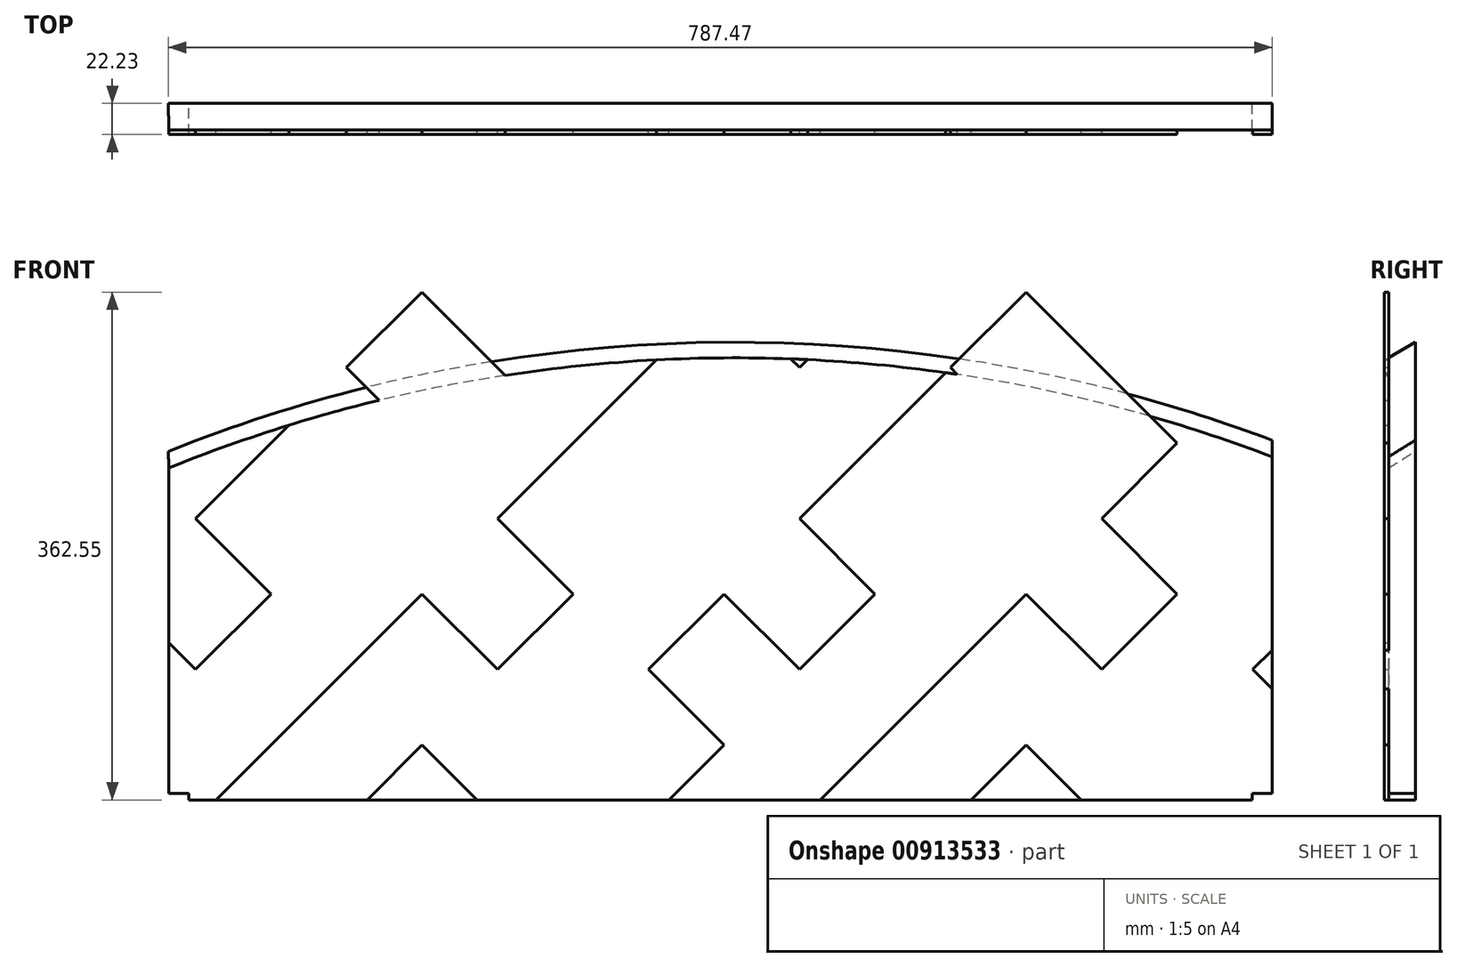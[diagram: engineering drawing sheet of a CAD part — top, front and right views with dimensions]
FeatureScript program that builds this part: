
annotation { "Feature Type Name" : "Feature", "Feature Type Description" : "" }
export const myFeature = defineFeature(function(context is Context, id is Id, definition is map)
    precondition{}
    {
        {
            var Q0;
            Q0=qCreatedBy(makeId("Front.planeOp"),FACE);
            var sketch = newSketch(context, id + "F0", { "sketchPlane" : qUnion([Q0])});
            skLineSegment(sketch, "E0.bottom", {"start": v(393.7, 124.62) * mm, "end": v(-393.67, 118.27) * mm, "construction": true});
            skLineSegment(sketch, "E0.top", {"start": v(379.41, -118.27) * mm, "end": v(-379.39, -118.27) * mm});
            skLineSegment(sketch, "E0.left", {"start": v(393.7, 124.62) * mm, "end": v(393.7, -113.5) * mm});
            skLineSegment(sketch, "E0.right", {"start": v(-393.67, 118.27) * mm, "end": v(-393.67, -113.5) * mm});
            skPoint(sketch, "E0.middle", {"position": v(0, 0) * mm});
            skLineSegment(sketch, "E1", {"start": v(379.41, -118.27) * mm, "end": v(379.41, -113.5) * mm});
            skLineSegment(sketch, "E2", {"start": v(379.41, -113.5) * mm, "end": v(393.7, -113.5) * mm});
            skPoint(sketch, "E3.orphan", {"position": v(393.67, -118.27) * mm});
            skLineSegment(sketch, "E4", {"start": v(-393.67, -113.5) * mm, "end": v(-379.39, -113.5) * mm});
            skLineSegment(sketch, "E5", {"start": v(-379.39, -113.5) * mm, "end": v(-379.39, -118.27) * mm});
            skLineSegment(sketch, "E6", {"start": v(0, 121.44) * mm, "end": v(-0.6, 196.06) * mm, "construction": true});
            skArc(sketch, "E7", {"start": v(393.7, 124.62) * mm, "mid": v(-0.59, 196.06) * mm, "end": v(-393.67, 118.27) * mm});
            skPoint(sketch, "E7.third.point", {"position": v(1080.75, -964.13) * mm});
            skLineSegment(sketch, "E8", {"start": v(-0.6, 196.06) * mm, "end": v(-0.6, 208.76) * mm, "construction": true});
            skLineSegment(sketch, "E9", {"start": v(-393.67, 118.27) * mm, "end": v(-393.78, 130.97) * mm});
            skLineSegment(sketch, "E10", {"start": v(393.7, 124.62) * mm, "end": v(393.7, 138.9) * mm});
            skArc(sketch, "E11", {"start": v(393.7, 138.9) * mm, "mid": v(-0.78, 208.75) * mm, "end": v(-393.78, 130.97) * mm});
            skSolve(sketch);
        }
        {
            var Q0;
            Q0=makeQuery(id+"F0.imprint","IMPRINT",FACE,{"disambiguationData":[TD([[makeQuery(id+"F0.imprint","IMPRINT",EDGE,{"derivedFrom":sQuery(id+"F0.wireOp",EDGE,"E0.top")}),-1.0]])]});
            var Q1;
            Q1=makeQuery(id+"F0.imprint","IMPRINT",FACE,{"disambiguationData":[TD([[makeQuery(id+"F0.imprint","IMPRINT",EDGE,{"derivedFrom":sQuery(id+"F0.wireOp",EDGE,"E7")}),-1.0]])]});
            extrude(context, id + "F1", {"entities" : qUnion([Q0, Q1]), "depth" : 19.05 * mm, "offsetDistance" : 25.4 * mm});
        }
        {
            var Q0;
            Q0=makeQuery(id+"F1.opExtrude","CAP_EDGE",EDGE,{"disambiguationData":[OSD([sQuery(id+"F0.wireOp",EDGE,"E11")])],"isStart":false});
            chamfer(context, id + "F2", {"entities" : qUnion([Q0]), "chamferType" : ChamferType.TWO_OFFSETS, "width1" : 19.56 * mm, "oppositeDirection" : true, "width2" : 11.43 * mm, "tangentPropagation" : true});
        }
        {
            var Q0;
            Q0=makeQuery(id+"F1.opExtrude","CAP_FACE",FACE,{"disambiguationData":[OSD([sQuery(id+"F0.wireOp",EDGE,"E0.top"),sQuery(id+"F0.wireOp",EDGE,"E0.left"),sQuery(id+"F0.wireOp",EDGE,"E0.right"),sQuery(id+"F0.wireOp",EDGE,"E1"),sQuery(id+"F0.wireOp",EDGE,"E2"),sQuery(id+"F0.wireOp",EDGE,"E4"),sQuery(id+"F0.wireOp",EDGE,"E5"),sQuery(id+"F0.wireOp",EDGE,"E9"),sQuery(id+"F0.wireOp",EDGE,"E10"),sQuery(id+"F0.wireOp",EDGE,"E11")])],"isStart":false});
            var sketch = newSketch(context, id + "F3", { "sketchPlane" : qUnion([Q0])});
            skLineSegment(sketch, "E12.bottom", {"start": v(272.06, -779.44) * mm, "end": v(325.94, -725.56) * mm});
            skLineSegment(sketch, "E12.top", {"start": v(164.3, -671.68) * mm, "end": v(218.17, -617.8) * mm});
            skLineSegment(sketch, "E12.left", {"start": v(272.06, -779.44) * mm, "end": v(164.3, -671.68) * mm});
            skLineSegment(sketch, "E12.right", {"start": v(325.94, -725.56) * mm, "end": v(218.17, -617.8) * mm});
            skLineSegment(sketch, "E13.bottom", {"start": v(433.7, -617.8) * mm, "end": v(379.82, -563.91) * mm});
            skLineSegment(sketch, "E13.top", {"start": v(325.94, -725.56) * mm, "end": v(272.06, -671.68) * mm});
            skLineSegment(sketch, "E13.left", {"start": v(433.7, -617.8) * mm, "end": v(325.94, -725.56) * mm});
            skLineSegment(sketch, "E13.right", {"start": v(379.82, -563.91) * mm, "end": v(272.06, -671.68) * mm});
            skLineSegment(sketch, "E14.bottom", {"start": v(272.06, -671.68) * mm, "end": v(325.94, -617.8) * mm});
            skLineSegment(sketch, "E14.top", {"start": v(164.3, -563.91) * mm, "end": v(218.17, -510.03) * mm});
            skLineSegment(sketch, "E14.left", {"start": v(272.06, -671.68) * mm, "end": v(164.3, -563.91) * mm});
            skLineSegment(sketch, "E14.right", {"start": v(325.94, -617.8) * mm, "end": v(218.17, -510.03) * mm});
            skPoint(sketch, "E15", {"position": v(325.94, -617.8) * mm});
            skLineSegment(sketch, "E16.bottom", {"start": v(272.06, -563.91) * mm, "end": v(325.94, -510.03) * mm});
            skLineSegment(sketch, "E16.top", {"start": v(164.3, -456.15) * mm, "end": v(218.17, -402.27) * mm});
            skLineSegment(sketch, "E16.left", {"start": v(272.06, -563.91) * mm, "end": v(164.3, -456.15) * mm});
            skLineSegment(sketch, "E16.right", {"start": v(325.94, -510.03) * mm, "end": v(218.17, -402.27) * mm});
            skLineSegment(sketch, "E17.bottom", {"start": v(433.7, -510.03) * mm, "end": v(379.82, -456.15) * mm});
            skLineSegment(sketch, "E17.top", {"start": v(325.94, -617.8) * mm, "end": v(272.06, -563.91) * mm});
            skLineSegment(sketch, "E17.left", {"start": v(433.7, -510.03) * mm, "end": v(325.94, -617.8) * mm});
            skLineSegment(sketch, "E17.right", {"start": v(379.82, -456.15) * mm, "end": v(272.06, -563.91) * mm});
            skLineSegment(sketch, "E18.bottom", {"start": v(272.06, -456.15) * mm, "end": v(325.94, -402.27) * mm});
            skLineSegment(sketch, "E18.top", {"start": v(164.3, -348.39) * mm, "end": v(218.17, -294.5) * mm});
            skLineSegment(sketch, "E18.left", {"start": v(272.06, -456.15) * mm, "end": v(164.3, -348.39) * mm});
            skLineSegment(sketch, "E18.right", {"start": v(325.94, -402.27) * mm, "end": v(218.17, -294.5) * mm});
            skLineSegment(sketch, "E19.bottom", {"start": v(433.7, -402.27) * mm, "end": v(379.82, -348.39) * mm});
            skLineSegment(sketch, "E19.top", {"start": v(325.94, -510.03) * mm, "end": v(272.06, -456.15) * mm});
            skLineSegment(sketch, "E19.left", {"start": v(433.7, -402.27) * mm, "end": v(325.94, -510.03) * mm});
            skLineSegment(sketch, "E19.right", {"start": v(379.82, -348.39) * mm, "end": v(272.06, -456.15) * mm});
            skLineSegment(sketch, "E20.bottom", {"start": v(487.58, -563.91) * mm, "end": v(541.46, -510.03) * mm});
            skLineSegment(sketch, "E20.top", {"start": v(379.82, -456.15) * mm, "end": v(433.7, -402.27) * mm});
            skLineSegment(sketch, "E20.left", {"start": v(487.58, -563.91) * mm, "end": v(379.82, -456.15) * mm});
            skLineSegment(sketch, "E20.right", {"start": v(541.46, -510.03) * mm, "end": v(433.7, -402.27) * mm});
            skLineSegment(sketch, "E21.bottom", {"start": v(487.58, -779.44) * mm, "end": v(541.46, -725.56) * mm});
            skLineSegment(sketch, "E21.top", {"start": v(379.82, -671.68) * mm, "end": v(433.7, -617.8) * mm});
            skLineSegment(sketch, "E21.left", {"start": v(487.58, -779.44) * mm, "end": v(379.82, -671.68) * mm});
            skLineSegment(sketch, "E21.right", {"start": v(541.46, -725.56) * mm, "end": v(433.7, -617.8) * mm});
            skLineSegment(sketch, "E22.bottom", {"start": v(487.58, -671.68) * mm, "end": v(541.46, -617.8) * mm});
            skLineSegment(sketch, "E22.top", {"start": v(379.82, -563.91) * mm, "end": v(433.7, -510.03) * mm});
            skLineSegment(sketch, "E22.left", {"start": v(487.58, -671.68) * mm, "end": v(379.82, -563.91) * mm});
            skLineSegment(sketch, "E22.right", {"start": v(541.46, -617.8) * mm, "end": v(433.7, -510.03) * mm});
            skLineSegment(sketch, "E23.bottom", {"start": v(272.06, -348.39) * mm, "end": v(325.94, -294.5) * mm});
            skLineSegment(sketch, "E23.top", {"start": v(164.3, -240.63) * mm, "end": v(218.17, -186.74) * mm});
            skLineSegment(sketch, "E23.left", {"start": v(272.06, -348.39) * mm, "end": v(164.3, -240.63) * mm});
            skLineSegment(sketch, "E23.right", {"start": v(325.94, -294.5) * mm, "end": v(218.17, -186.74) * mm});
            skLineSegment(sketch, "E24.bottom", {"start": v(433.7, -294.5) * mm, "end": v(379.82, -240.63) * mm});
            skLineSegment(sketch, "E24.top", {"start": v(325.94, -402.27) * mm, "end": v(272.06, -348.39) * mm});
            skLineSegment(sketch, "E24.left", {"start": v(433.7, -294.5) * mm, "end": v(325.94, -402.27) * mm});
            skLineSegment(sketch, "E24.right", {"start": v(379.82, -240.63) * mm, "end": v(272.06, -348.39) * mm});
            skLineSegment(sketch, "E25.bottom", {"start": v(218.17, -402.27) * mm, "end": v(164.3, -348.39) * mm});
            skLineSegment(sketch, "E25.top", {"start": v(110.41, -510.03) * mm, "end": v(56.53, -456.15) * mm});
            skLineSegment(sketch, "E25.left", {"start": v(218.17, -402.27) * mm, "end": v(110.41, -510.03) * mm});
            skLineSegment(sketch, "E25.right", {"start": v(164.3, -348.39) * mm, "end": v(56.53, -456.15) * mm});
            skLineSegment(sketch, "E26.bottom", {"start": v(218.17, -294.5) * mm, "end": v(164.3, -240.63) * mm});
            skLineSegment(sketch, "E26.top", {"start": v(110.41, -402.27) * mm, "end": v(56.53, -348.39) * mm});
            skLineSegment(sketch, "E26.left", {"start": v(218.17, -294.5) * mm, "end": v(110.41, -402.27) * mm});
            skLineSegment(sketch, "E26.right", {"start": v(164.3, -240.63) * mm, "end": v(56.53, -348.39) * mm});
            skLineSegment(sketch, "E27.bottom", {"start": v(218.17, -617.8) * mm, "end": v(164.3, -563.91) * mm});
            skLineSegment(sketch, "E27.top", {"start": v(110.41, -725.56) * mm, "end": v(56.53, -671.68) * mm});
            skLineSegment(sketch, "E27.left", {"start": v(218.17, -617.8) * mm, "end": v(110.41, -725.56) * mm});
            skLineSegment(sketch, "E27.right", {"start": v(164.3, -563.91) * mm, "end": v(56.53, -671.68) * mm});
            skLineSegment(sketch, "E28.bottom", {"start": v(218.17, -510.03) * mm, "end": v(164.3, -456.15) * mm});
            skLineSegment(sketch, "E28.top", {"start": v(110.41, -617.8) * mm, "end": v(56.53, -563.91) * mm});
            skLineSegment(sketch, "E28.left", {"start": v(218.17, -510.03) * mm, "end": v(110.41, -617.8) * mm});
            skLineSegment(sketch, "E28.right", {"start": v(164.3, -456.15) * mm, "end": v(56.53, -563.91) * mm});
            skLineSegment(sketch, "E29.bottom", {"start": v(272.09, -240.66) * mm, "end": v(325.97, -186.77) * mm});
            skLineSegment(sketch, "E29.top", {"start": v(164.32, -132.9) * mm, "end": v(218.2, -79.01) * mm});
            skLineSegment(sketch, "E29.left", {"start": v(272.09, -240.66) * mm, "end": v(164.32, -132.9) * mm});
            skLineSegment(sketch, "E29.right", {"start": v(325.97, -186.77) * mm, "end": v(218.2, -79.01) * mm});
            skLineSegment(sketch, "E30.bottom", {"start": v(433.73, -79.01) * mm, "end": v(379.85, -25.13) * mm});
            skLineSegment(sketch, "E30.top", {"start": v(325.97, -186.77) * mm, "end": v(272.09, -132.9) * mm});
            skLineSegment(sketch, "E30.left", {"start": v(433.73, -79.01) * mm, "end": v(325.97, -186.77) * mm});
            skLineSegment(sketch, "E30.right", {"start": v(379.85, -25.13) * mm, "end": v(272.09, -132.9) * mm});
            skLineSegment(sketch, "E31.bottom", {"start": v(272.09, -132.9) * mm, "end": v(325.97, -79.01) * mm});
            skLineSegment(sketch, "E31.top", {"start": v(164.32, -25.13) * mm, "end": v(218.2, 28.75) * mm});
            skLineSegment(sketch, "E31.left", {"start": v(272.09, -132.9) * mm, "end": v(164.32, -25.13) * mm});
            skLineSegment(sketch, "E31.right", {"start": v(325.97, -79.01) * mm, "end": v(218.2, 28.75) * mm});
            skPoint(sketch, "E32", {"position": v(325.97, -79.01) * mm});
            skLineSegment(sketch, "E33.bottom", {"start": v(272.09, -25.13) * mm, "end": v(325.97, 28.75) * mm});
            skLineSegment(sketch, "E33.top", {"start": v(164.32, 82.63) * mm, "end": v(218.2, 136.52) * mm});
            skLineSegment(sketch, "E33.left", {"start": v(272.09, -25.13) * mm, "end": v(164.32, 82.63) * mm});
            skLineSegment(sketch, "E33.right", {"start": v(325.97, 28.75) * mm, "end": v(218.2, 136.52) * mm});
            skLineSegment(sketch, "E34.bottom", {"start": v(433.73, 28.75) * mm, "end": v(379.85, 82.63) * mm});
            skLineSegment(sketch, "E34.top", {"start": v(325.97, -79.01) * mm, "end": v(272.09, -25.13) * mm});
            skLineSegment(sketch, "E34.left", {"start": v(433.73, 28.75) * mm, "end": v(325.97, -79.01) * mm});
            skLineSegment(sketch, "E34.right", {"start": v(379.85, 82.63) * mm, "end": v(272.09, -25.13) * mm});
            skLineSegment(sketch, "E35.bottom", {"start": v(272.09, 82.63) * mm, "end": v(325.97, 136.52) * mm});
            skLineSegment(sketch, "E35.top", {"start": v(164.32, 190.4) * mm, "end": v(218.2, 244.28) * mm});
            skLineSegment(sketch, "E35.left", {"start": v(272.09, 82.63) * mm, "end": v(164.32, 190.4) * mm});
            skLineSegment(sketch, "E35.right", {"start": v(325.97, 136.52) * mm, "end": v(218.2, 244.28) * mm});
            skLineSegment(sketch, "E36.bottom", {"start": v(433.73, 136.52) * mm, "end": v(379.85, 190.4) * mm});
            skLineSegment(sketch, "E36.top", {"start": v(325.97, 28.75) * mm, "end": v(272.09, 82.63) * mm});
            skLineSegment(sketch, "E36.left", {"start": v(433.73, 136.52) * mm, "end": v(325.97, 28.75) * mm});
            skLineSegment(sketch, "E36.right", {"start": v(379.85, 190.4) * mm, "end": v(272.09, 82.63) * mm});
            skLineSegment(sketch, "E37.bottom", {"start": v(487.61, -25.13) * mm, "end": v(541.5, 28.75) * mm});
            skLineSegment(sketch, "E37.top", {"start": v(379.85, 82.63) * mm, "end": v(433.73, 136.52) * mm});
            skLineSegment(sketch, "E37.left", {"start": v(487.61, -25.13) * mm, "end": v(379.85, 82.63) * mm});
            skLineSegment(sketch, "E37.right", {"start": v(541.5, 28.75) * mm, "end": v(433.73, 136.52) * mm});
            skLineSegment(sketch, "E38.bottom", {"start": v(487.61, -240.66) * mm, "end": v(541.5, -186.77) * mm});
            skLineSegment(sketch, "E38.top", {"start": v(379.85, -132.9) * mm, "end": v(433.73, -79.01) * mm});
            skLineSegment(sketch, "E38.left", {"start": v(487.61, -240.66) * mm, "end": v(379.85, -132.9) * mm});
            skLineSegment(sketch, "E38.right", {"start": v(541.5, -186.77) * mm, "end": v(433.73, -79.01) * mm});
            skLineSegment(sketch, "E39.bottom", {"start": v(487.61, -132.9) * mm, "end": v(541.5, -79.01) * mm});
            skLineSegment(sketch, "E39.top", {"start": v(379.85, -25.13) * mm, "end": v(433.73, 28.75) * mm});
            skLineSegment(sketch, "E39.left", {"start": v(487.61, -132.9) * mm, "end": v(379.85, -25.13) * mm});
            skLineSegment(sketch, "E39.right", {"start": v(541.5, -79.01) * mm, "end": v(433.73, 28.75) * mm});
            skLineSegment(sketch, "E40.bottom", {"start": v(272.09, 190.4) * mm, "end": v(325.97, 244.28) * mm});
            skLineSegment(sketch, "E40.top", {"start": v(164.32, 298.16) * mm, "end": v(218.2, 352.04) * mm});
            skLineSegment(sketch, "E40.left", {"start": v(272.09, 190.4) * mm, "end": v(164.32, 298.16) * mm});
            skLineSegment(sketch, "E40.right", {"start": v(325.97, 244.28) * mm, "end": v(218.2, 352.04) * mm});
            skLineSegment(sketch, "E41.bottom", {"start": v(433.73, 244.28) * mm, "end": v(379.85, 298.16) * mm});
            skLineSegment(sketch, "E41.top", {"start": v(325.97, 136.52) * mm, "end": v(272.09, 190.4) * mm});
            skLineSegment(sketch, "E41.left", {"start": v(433.73, 244.28) * mm, "end": v(325.97, 136.52) * mm});
            skLineSegment(sketch, "E41.right", {"start": v(379.85, 298.16) * mm, "end": v(272.09, 190.4) * mm});
            skLineSegment(sketch, "E42.bottom", {"start": v(218.2, 136.52) * mm, "end": v(164.32, 190.4) * mm});
            skLineSegment(sketch, "E42.top", {"start": v(110.44, 28.75) * mm, "end": v(56.56, 82.63) * mm});
            skLineSegment(sketch, "E42.left", {"start": v(218.2, 136.52) * mm, "end": v(110.44, 28.75) * mm});
            skLineSegment(sketch, "E42.right", {"start": v(164.32, 190.4) * mm, "end": v(56.56, 82.63) * mm});
            skLineSegment(sketch, "E43.bottom", {"start": v(218.2, 244.28) * mm, "end": v(164.32, 298.16) * mm});
            skLineSegment(sketch, "E43.top", {"start": v(110.44, 136.52) * mm, "end": v(56.56, 190.4) * mm});
            skLineSegment(sketch, "E43.left", {"start": v(218.2, 244.28) * mm, "end": v(110.44, 136.52) * mm});
            skLineSegment(sketch, "E43.right", {"start": v(164.32, 298.16) * mm, "end": v(56.56, 190.4) * mm});
            skLineSegment(sketch, "E44.bottom", {"start": v(218.2, -79.01) * mm, "end": v(164.32, -25.13) * mm});
            skLineSegment(sketch, "E44.top", {"start": v(110.44, -186.77) * mm, "end": v(56.56, -132.9) * mm});
            skLineSegment(sketch, "E44.left", {"start": v(218.2, -79.01) * mm, "end": v(110.44, -186.77) * mm});
            skLineSegment(sketch, "E44.right", {"start": v(164.32, -25.13) * mm, "end": v(56.56, -132.9) * mm});
            skLineSegment(sketch, "E45.bottom", {"start": v(218.2, 28.75) * mm, "end": v(164.32, 82.63) * mm});
            skLineSegment(sketch, "E45.top", {"start": v(110.44, -79.01) * mm, "end": v(56.56, -25.13) * mm});
            skLineSegment(sketch, "E45.left", {"start": v(218.2, 28.75) * mm, "end": v(110.44, -79.01) * mm});
            skLineSegment(sketch, "E45.right", {"start": v(164.32, 82.63) * mm, "end": v(56.56, -25.13) * mm});
            skLineSegment(sketch, "E46.bottom", {"start": v(433.7, -186.74) * mm, "end": v(379.82, -132.86) * mm});
            skLineSegment(sketch, "E46.top", {"start": v(325.94, -294.5) * mm, "end": v(272.06, -240.63) * mm});
            skLineSegment(sketch, "E46.left", {"start": v(433.7, -186.74) * mm, "end": v(325.94, -294.5) * mm});
            skLineSegment(sketch, "E46.right", {"start": v(379.82, -132.86) * mm, "end": v(272.06, -240.63) * mm});
            skLineSegment(sketch, "E47.bottom", {"start": v(-159, -779.44) * mm, "end": v(-105.11, -725.56) * mm});
            skLineSegment(sketch, "E47.top", {"start": v(-266.76, -671.68) * mm, "end": v(-212.88, -617.8) * mm});
            skLineSegment(sketch, "E47.left", {"start": v(-159, -779.44) * mm, "end": v(-266.76, -671.68) * mm});
            skLineSegment(sketch, "E47.right", {"start": v(-105.11, -725.56) * mm, "end": v(-212.88, -617.8) * mm});
            skLineSegment(sketch, "E48.bottom", {"start": v(2.65, -617.8) * mm, "end": v(-51.23, -563.91) * mm});
            skLineSegment(sketch, "E48.top", {"start": v(-105.11, -725.56) * mm, "end": v(-159, -671.68) * mm});
            skLineSegment(sketch, "E48.left", {"start": v(2.65, -617.8) * mm, "end": v(-105.11, -725.56) * mm});
            skLineSegment(sketch, "E48.right", {"start": v(-51.23, -563.91) * mm, "end": v(-159, -671.68) * mm});
            skLineSegment(sketch, "E49.bottom", {"start": v(-159, -671.68) * mm, "end": v(-105.11, -617.8) * mm});
            skLineSegment(sketch, "E49.top", {"start": v(-266.76, -563.91) * mm, "end": v(-212.88, -510.03) * mm});
            skLineSegment(sketch, "E49.left", {"start": v(-159, -671.68) * mm, "end": v(-266.76, -563.91) * mm});
            skLineSegment(sketch, "E49.right", {"start": v(-105.11, -617.8) * mm, "end": v(-212.88, -510.03) * mm});
            skPoint(sketch, "E50", {"position": v(-105.11, -617.8) * mm});
            skLineSegment(sketch, "E51.bottom", {"start": v(-159, -563.91) * mm, "end": v(-105.11, -510.03) * mm});
            skLineSegment(sketch, "E51.top", {"start": v(-266.76, -456.15) * mm, "end": v(-212.88, -402.27) * mm});
            skLineSegment(sketch, "E51.left", {"start": v(-159, -563.91) * mm, "end": v(-266.76, -456.15) * mm});
            skLineSegment(sketch, "E51.right", {"start": v(-105.11, -510.03) * mm, "end": v(-212.88, -402.27) * mm});
            skLineSegment(sketch, "E52.bottom", {"start": v(2.65, -510.03) * mm, "end": v(-51.23, -456.15) * mm});
            skLineSegment(sketch, "E52.top", {"start": v(-105.11, -617.8) * mm, "end": v(-159, -563.91) * mm});
            skLineSegment(sketch, "E52.left", {"start": v(2.65, -510.03) * mm, "end": v(-105.11, -617.8) * mm});
            skLineSegment(sketch, "E52.right", {"start": v(-51.23, -456.15) * mm, "end": v(-159, -563.91) * mm});
            skLineSegment(sketch, "E53.bottom", {"start": v(-159, -456.15) * mm, "end": v(-105.11, -402.27) * mm});
            skLineSegment(sketch, "E53.top", {"start": v(-266.76, -348.39) * mm, "end": v(-212.88, -294.5) * mm});
            skLineSegment(sketch, "E53.left", {"start": v(-159, -456.15) * mm, "end": v(-266.76, -348.39) * mm});
            skLineSegment(sketch, "E53.right", {"start": v(-105.11, -402.27) * mm, "end": v(-212.88, -294.5) * mm});
            skLineSegment(sketch, "E54.bottom", {"start": v(2.65, -402.27) * mm, "end": v(-51.23, -348.39) * mm});
            skLineSegment(sketch, "E54.top", {"start": v(-105.11, -510.03) * mm, "end": v(-159, -456.15) * mm});
            skLineSegment(sketch, "E54.left", {"start": v(2.65, -402.27) * mm, "end": v(-105.11, -510.03) * mm});
            skLineSegment(sketch, "E54.right", {"start": v(-51.23, -348.39) * mm, "end": v(-159, -456.15) * mm});
            skLineSegment(sketch, "E55.bottom", {"start": v(56.53, -563.91) * mm, "end": v(110.41, -510.03) * mm});
            skLineSegment(sketch, "E55.top", {"start": v(-51.23, -456.15) * mm, "end": v(2.65, -402.27) * mm});
            skLineSegment(sketch, "E55.left", {"start": v(56.53, -563.91) * mm, "end": v(-51.23, -456.15) * mm});
            skLineSegment(sketch, "E55.right", {"start": v(110.41, -510.03) * mm, "end": v(2.65, -402.27) * mm});
            skLineSegment(sketch, "E56.bottom", {"start": v(56.53, -779.44) * mm, "end": v(110.41, -725.56) * mm});
            skLineSegment(sketch, "E56.top", {"start": v(-51.23, -671.68) * mm, "end": v(2.65, -617.8) * mm});
            skLineSegment(sketch, "E56.left", {"start": v(56.53, -779.44) * mm, "end": v(-51.23, -671.68) * mm});
            skLineSegment(sketch, "E56.right", {"start": v(110.41, -725.56) * mm, "end": v(2.65, -617.8) * mm});
            skLineSegment(sketch, "E57.bottom", {"start": v(56.53, -671.68) * mm, "end": v(110.41, -617.8) * mm});
            skLineSegment(sketch, "E57.top", {"start": v(-51.23, -563.91) * mm, "end": v(2.65, -510.03) * mm});
            skLineSegment(sketch, "E57.left", {"start": v(56.53, -671.68) * mm, "end": v(-51.23, -563.91) * mm});
            skLineSegment(sketch, "E57.right", {"start": v(110.41, -617.8) * mm, "end": v(2.65, -510.03) * mm});
            skLineSegment(sketch, "E58.bottom", {"start": v(-159, -348.39) * mm, "end": v(-105.11, -294.5) * mm});
            skLineSegment(sketch, "E58.top", {"start": v(-266.76, -240.63) * mm, "end": v(-212.88, -186.74) * mm});
            skLineSegment(sketch, "E58.left", {"start": v(-159, -348.39) * mm, "end": v(-266.76, -240.63) * mm});
            skLineSegment(sketch, "E58.right", {"start": v(-105.11, -294.5) * mm, "end": v(-212.88, -186.74) * mm});
            skLineSegment(sketch, "E59.bottom", {"start": v(2.65, -294.5) * mm, "end": v(-51.23, -240.63) * mm});
            skLineSegment(sketch, "E59.top", {"start": v(-105.11, -402.27) * mm, "end": v(-159, -348.39) * mm});
            skLineSegment(sketch, "E59.left", {"start": v(2.65, -294.5) * mm, "end": v(-105.11, -402.27) * mm});
            skLineSegment(sketch, "E59.right", {"start": v(-51.23, -240.63) * mm, "end": v(-159, -348.39) * mm});
            skLineSegment(sketch, "E60.bottom", {"start": v(-212.88, -402.27) * mm, "end": v(-266.76, -348.39) * mm});
            skLineSegment(sketch, "E60.top", {"start": v(-320.64, -510.03) * mm, "end": v(-374.52, -456.15) * mm});
            skLineSegment(sketch, "E60.left", {"start": v(-212.88, -402.27) * mm, "end": v(-320.64, -510.03) * mm});
            skLineSegment(sketch, "E60.right", {"start": v(-266.76, -348.39) * mm, "end": v(-374.52, -456.15) * mm});
            skLineSegment(sketch, "E61.bottom", {"start": v(-212.88, -294.5) * mm, "end": v(-266.76, -240.63) * mm});
            skLineSegment(sketch, "E61.top", {"start": v(-320.64, -402.27) * mm, "end": v(-374.52, -348.39) * mm});
            skLineSegment(sketch, "E61.left", {"start": v(-212.88, -294.5) * mm, "end": v(-320.64, -402.27) * mm});
            skLineSegment(sketch, "E61.right", {"start": v(-266.76, -240.63) * mm, "end": v(-374.52, -348.39) * mm});
            skLineSegment(sketch, "E62.bottom", {"start": v(-212.88, -617.8) * mm, "end": v(-266.76, -563.91) * mm});
            skLineSegment(sketch, "E62.top", {"start": v(-320.64, -725.56) * mm, "end": v(-374.52, -671.68) * mm});
            skLineSegment(sketch, "E62.left", {"start": v(-212.88, -617.8) * mm, "end": v(-320.64, -725.56) * mm});
            skLineSegment(sketch, "E62.right", {"start": v(-266.76, -563.91) * mm, "end": v(-374.52, -671.68) * mm});
            skLineSegment(sketch, "E63.bottom", {"start": v(-212.88, -510.03) * mm, "end": v(-266.76, -456.15) * mm});
            skLineSegment(sketch, "E63.top", {"start": v(-320.64, -617.8) * mm, "end": v(-374.52, -563.91) * mm});
            skLineSegment(sketch, "E63.left", {"start": v(-212.88, -510.03) * mm, "end": v(-320.64, -617.8) * mm});
            skLineSegment(sketch, "E63.right", {"start": v(-266.76, -456.15) * mm, "end": v(-374.52, -563.91) * mm});
            skLineSegment(sketch, "E64.bottom", {"start": v(-158.97, -240.66) * mm, "end": v(-105.08, -186.77) * mm});
            skLineSegment(sketch, "E64.top", {"start": v(-266.73, -132.9) * mm, "end": v(-212.85, -79.01) * mm});
            skLineSegment(sketch, "E64.left", {"start": v(-158.97, -240.66) * mm, "end": v(-266.73, -132.9) * mm});
            skLineSegment(sketch, "E64.right", {"start": v(-105.08, -186.77) * mm, "end": v(-212.85, -79.01) * mm});
            skLineSegment(sketch, "E65.bottom", {"start": v(2.68, -79.01) * mm, "end": v(-51.2, -25.13) * mm});
            skLineSegment(sketch, "E65.top", {"start": v(-105.08, -186.77) * mm, "end": v(-158.97, -132.9) * mm});
            skLineSegment(sketch, "E65.left", {"start": v(2.68, -79.01) * mm, "end": v(-105.08, -186.77) * mm});
            skLineSegment(sketch, "E65.right", {"start": v(-51.2, -25.13) * mm, "end": v(-158.97, -132.9) * mm});
            skLineSegment(sketch, "E66.bottom", {"start": v(-158.97, -132.9) * mm, "end": v(-105.08, -79.01) * mm});
            skLineSegment(sketch, "E66.top", {"start": v(-266.73, -25.13) * mm, "end": v(-212.85, 28.75) * mm});
            skLineSegment(sketch, "E66.left", {"start": v(-158.97, -132.9) * mm, "end": v(-266.73, -25.13) * mm});
            skLineSegment(sketch, "E66.right", {"start": v(-105.08, -79.01) * mm, "end": v(-212.85, 28.75) * mm});
            skPoint(sketch, "E67", {"position": v(-105.08, -79.01) * mm});
            skLineSegment(sketch, "E68.bottom", {"start": v(-158.97, -25.13) * mm, "end": v(-105.08, 28.75) * mm});
            skLineSegment(sketch, "E68.top", {"start": v(-266.73, 82.63) * mm, "end": v(-212.85, 136.52) * mm});
            skLineSegment(sketch, "E68.left", {"start": v(-158.97, -25.13) * mm, "end": v(-266.73, 82.63) * mm});
            skLineSegment(sketch, "E68.right", {"start": v(-105.08, 28.75) * mm, "end": v(-212.85, 136.52) * mm});
            skLineSegment(sketch, "E69.bottom", {"start": v(2.68, 28.75) * mm, "end": v(-51.2, 82.63) * mm});
            skLineSegment(sketch, "E69.top", {"start": v(-105.08, -79.01) * mm, "end": v(-158.97, -25.13) * mm});
            skLineSegment(sketch, "E69.left", {"start": v(2.68, 28.75) * mm, "end": v(-105.08, -79.01) * mm});
            skLineSegment(sketch, "E69.right", {"start": v(-51.2, 82.63) * mm, "end": v(-158.97, -25.13) * mm});
            skLineSegment(sketch, "E70.bottom", {"start": v(-158.97, 82.63) * mm, "end": v(-105.08, 136.52) * mm});
            skLineSegment(sketch, "E70.top", {"start": v(-266.73, 190.4) * mm, "end": v(-212.85, 244.28) * mm});
            skLineSegment(sketch, "E70.left", {"start": v(-158.97, 82.63) * mm, "end": v(-266.73, 190.4) * mm});
            skLineSegment(sketch, "E70.right", {"start": v(-105.08, 136.52) * mm, "end": v(-212.85, 244.28) * mm});
            skLineSegment(sketch, "E71.bottom", {"start": v(2.68, 136.52) * mm, "end": v(-51.2, 190.4) * mm});
            skLineSegment(sketch, "E71.top", {"start": v(-105.08, 28.75) * mm, "end": v(-158.97, 82.63) * mm});
            skLineSegment(sketch, "E71.left", {"start": v(2.68, 136.52) * mm, "end": v(-105.08, 28.75) * mm});
            skLineSegment(sketch, "E71.right", {"start": v(-51.2, 190.4) * mm, "end": v(-158.97, 82.63) * mm});
            skLineSegment(sketch, "E72.bottom", {"start": v(56.56, -25.13) * mm, "end": v(110.44, 28.75) * mm});
            skLineSegment(sketch, "E72.top", {"start": v(-51.2, 82.63) * mm, "end": v(2.68, 136.52) * mm});
            skLineSegment(sketch, "E72.left", {"start": v(56.56, -25.13) * mm, "end": v(-51.2, 82.63) * mm});
            skLineSegment(sketch, "E72.right", {"start": v(110.44, 28.75) * mm, "end": v(2.68, 136.52) * mm});
            skLineSegment(sketch, "E73.bottom", {"start": v(56.56, -240.66) * mm, "end": v(110.44, -186.77) * mm});
            skLineSegment(sketch, "E73.top", {"start": v(-51.2, -132.9) * mm, "end": v(2.68, -79.01) * mm});
            skLineSegment(sketch, "E73.left", {"start": v(56.56, -240.66) * mm, "end": v(-51.2, -132.9) * mm});
            skLineSegment(sketch, "E73.right", {"start": v(110.44, -186.77) * mm, "end": v(2.68, -79.01) * mm});
            skLineSegment(sketch, "E74.bottom", {"start": v(56.56, -132.9) * mm, "end": v(110.44, -79.01) * mm});
            skLineSegment(sketch, "E74.top", {"start": v(-51.2, -25.13) * mm, "end": v(2.68, 28.75) * mm});
            skLineSegment(sketch, "E74.left", {"start": v(56.56, -132.9) * mm, "end": v(-51.2, -25.13) * mm});
            skLineSegment(sketch, "E74.right", {"start": v(110.44, -79.01) * mm, "end": v(2.68, 28.75) * mm});
            skLineSegment(sketch, "E75.bottom", {"start": v(-158.97, 190.4) * mm, "end": v(-105.08, 244.28) * mm});
            skLineSegment(sketch, "E75.top", {"start": v(-266.73, 298.16) * mm, "end": v(-212.85, 352.04) * mm});
            skLineSegment(sketch, "E75.left", {"start": v(-158.97, 190.4) * mm, "end": v(-266.73, 298.16) * mm});
            skLineSegment(sketch, "E75.right", {"start": v(-105.08, 244.28) * mm, "end": v(-212.85, 352.04) * mm});
            skLineSegment(sketch, "E76.bottom", {"start": v(2.68, 244.28) * mm, "end": v(-51.2, 298.16) * mm});
            skLineSegment(sketch, "E76.top", {"start": v(-105.08, 136.52) * mm, "end": v(-158.97, 190.4) * mm});
            skLineSegment(sketch, "E76.left", {"start": v(2.68, 244.28) * mm, "end": v(-105.08, 136.52) * mm});
            skLineSegment(sketch, "E76.right", {"start": v(-51.2, 298.16) * mm, "end": v(-158.97, 190.4) * mm});
            skLineSegment(sketch, "E77.bottom", {"start": v(-212.85, 136.52) * mm, "end": v(-266.73, 190.4) * mm});
            skLineSegment(sketch, "E77.top", {"start": v(-320.61, 28.75) * mm, "end": v(-374.5, 82.63) * mm});
            skLineSegment(sketch, "E77.left", {"start": v(-212.85, 136.52) * mm, "end": v(-320.61, 28.75) * mm});
            skLineSegment(sketch, "E77.right", {"start": v(-266.73, 190.4) * mm, "end": v(-374.5, 82.63) * mm});
            skLineSegment(sketch, "E78.bottom", {"start": v(-212.85, 244.28) * mm, "end": v(-266.73, 298.16) * mm});
            skLineSegment(sketch, "E78.top", {"start": v(-320.61, 136.52) * mm, "end": v(-374.5, 190.4) * mm});
            skLineSegment(sketch, "E78.left", {"start": v(-212.85, 244.28) * mm, "end": v(-320.61, 136.52) * mm});
            skLineSegment(sketch, "E78.right", {"start": v(-266.73, 298.16) * mm, "end": v(-374.5, 190.4) * mm});
            skLineSegment(sketch, "E79.bottom", {"start": v(-212.85, -79.01) * mm, "end": v(-266.73, -25.13) * mm});
            skLineSegment(sketch, "E79.top", {"start": v(-320.61, -186.77) * mm, "end": v(-374.5, -132.9) * mm});
            skLineSegment(sketch, "E79.left", {"start": v(-212.85, -79.01) * mm, "end": v(-320.61, -186.77) * mm});
            skLineSegment(sketch, "E79.right", {"start": v(-266.73, -25.13) * mm, "end": v(-374.5, -132.9) * mm});
            skLineSegment(sketch, "E80.bottom", {"start": v(-212.85, 28.75) * mm, "end": v(-266.73, 82.63) * mm});
            skLineSegment(sketch, "E80.top", {"start": v(-320.61, -79.01) * mm, "end": v(-374.5, -25.13) * mm});
            skLineSegment(sketch, "E80.left", {"start": v(-212.85, 28.75) * mm, "end": v(-320.61, -79.01) * mm});
            skLineSegment(sketch, "E80.right", {"start": v(-266.73, 82.63) * mm, "end": v(-374.5, -25.13) * mm});
            skLineSegment(sketch, "E81.bottom", {"start": v(2.65, -186.74) * mm, "end": v(-51.23, -132.86) * mm});
            skLineSegment(sketch, "E81.top", {"start": v(-105.11, -294.5) * mm, "end": v(-159, -240.63) * mm});
            skLineSegment(sketch, "E81.left", {"start": v(2.65, -186.74) * mm, "end": v(-105.11, -294.5) * mm});
            skLineSegment(sketch, "E81.right", {"start": v(-51.23, -132.86) * mm, "end": v(-159, -240.63) * mm});
            skLineSegment(sketch, "E82.bottom", {"start": v(56.53, -456.15) * mm, "end": v(110.41, -402.27) * mm});
            skLineSegment(sketch, "E82.left", {"start": v(56.53, -456.15) * mm, "end": v(-51.23, -348.39) * mm});
            skLineSegment(sketch, "E82.right", {"start": v(110.41, -402.27) * mm, "end": v(2.65, -294.5) * mm});
            skLineSegment(sketch, "E83", {"start": v(-51.23, -348.39) * mm, "end": v(2.65, -294.5) * mm});
            skLineSegment(sketch, "E84.bottom", {"start": v(56.56, 82.63) * mm, "end": v(110.44, 136.52) * mm});
            skLineSegment(sketch, "E84.left", {"start": v(56.56, 82.63) * mm, "end": v(-51.2, 190.4) * mm});
            skLineSegment(sketch, "E84.right", {"start": v(110.44, 136.52) * mm, "end": v(2.68, 244.28) * mm});
            skLineSegment(sketch, "E85", {"start": v(-51.2, 190.4) * mm, "end": v(2.68, 244.28) * mm});
            skLineSegment(sketch, "E86.bottom", {"start": v(487.58, -456.15) * mm, "end": v(541.46, -402.27) * mm});
            skLineSegment(sketch, "E86.left", {"start": v(487.58, -456.15) * mm, "end": v(379.82, -348.39) * mm});
            skLineSegment(sketch, "E86.right", {"start": v(541.46, -402.27) * mm, "end": v(433.7, -294.5) * mm});
            skLineSegment(sketch, "E87", {"start": v(379.82, -348.39) * mm, "end": v(433.7, -294.5) * mm});
            skLineSegment(sketch, "E88.bottom", {"start": v(56.53, -348.39) * mm, "end": v(110.41, -294.5) * mm});
            skLineSegment(sketch, "E88.left", {"start": v(56.53, -348.39) * mm, "end": v(-51.23, -240.63) * mm});
            skLineSegment(sketch, "E88.right", {"start": v(110.41, -294.5) * mm, "end": v(2.65, -186.74) * mm});
            skLineSegment(sketch, "E89", {"start": v(-51.23, -240.63) * mm, "end": v(2.65, -186.74) * mm});
            skLineSegment(sketch, "E90.bottom", {"start": v(218.2, -186.77) * mm, "end": v(164.32, -132.9) * mm});
            skLineSegment(sketch, "E90.left", {"start": v(218.2, -186.77) * mm, "end": v(110.44, -294.54) * mm});
            skLineSegment(sketch, "E90.right", {"start": v(164.32, -132.9) * mm, "end": v(56.56, -240.66) * mm});
            skLineSegment(sketch, "E91", {"start": v(110.44, -294.54) * mm, "end": v(56.56, -240.66) * mm});
            skLineSegment(sketch, "E92.bottom", {"start": v(487.58, -348.39) * mm, "end": v(541.46, -294.5) * mm});
            skLineSegment(sketch, "E92.left", {"start": v(487.58, -348.39) * mm, "end": v(379.82, -240.63) * mm});
            skLineSegment(sketch, "E92.right", {"start": v(541.46, -294.5) * mm, "end": v(433.7, -186.74) * mm});
            skLineSegment(sketch, "E93", {"start": v(379.82, -240.63) * mm, "end": v(433.7, -186.74) * mm});
            skLineSegment(sketch, "E94.bottom", {"start": v(487.61, 82.63) * mm, "end": v(541.5, 136.52) * mm});
            skLineSegment(sketch, "E94.left", {"start": v(487.61, 82.63) * mm, "end": v(379.85, 190.4) * mm});
            skLineSegment(sketch, "E94.right", {"start": v(541.5, 136.52) * mm, "end": v(433.73, 244.28) * mm});
            skLineSegment(sketch, "E95", {"start": v(379.85, 190.4) * mm, "end": v(433.73, 244.28) * mm});
            skLineSegment(sketch, "E96", {"start": v(-374.52, -132.86) * mm, "end": v(-320.64, -78.98) * mm});
            skLineSegment(sketch, "E97.bottom", {"start": v(56.56, 190.4) * mm, "end": v(110.44, 244.28) * mm});
            skLineSegment(sketch, "E97.left", {"start": v(56.56, 190.4) * mm, "end": v(-51.2, 298.16) * mm});
            skLineSegment(sketch, "E97.right", {"start": v(110.44, 244.28) * mm, "end": v(2.68, 352.04) * mm});
            skLineSegment(sketch, "E98", {"start": v(-51.2, 298.16) * mm, "end": v(2.68, 352.04) * mm});
            skLineSegment(sketch, "E99.bottom", {"start": v(-266.76, -132.86) * mm, "end": v(-212.88, -186.74) * mm});
            skLineSegment(sketch, "E99.top", {"start": v(-374.52, -240.63) * mm, "end": v(-320.64, -294.5) * mm});
            skLineSegment(sketch, "E99.left", {"start": v(-266.76, -132.86) * mm, "end": v(-374.52, -240.63) * mm});
            skLineSegment(sketch, "E99.right", {"start": v(-212.88, -186.74) * mm, "end": v(-320.64, -294.5) * mm});
            skLineSegment(sketch, "E100.bottom", {"start": v(-482.25, -25.13) * mm, "end": v(-428.37, 28.75) * mm});
            skLineSegment(sketch, "E100.top", {"start": v(-374.5, -132.9) * mm, "end": v(-320.61, -79.01) * mm});
            skLineSegment(sketch, "E100.left", {"start": v(-482.25, -25.13) * mm, "end": v(-374.5, -132.9) * mm});
            skLineSegment(sketch, "E100.right", {"start": v(-428.37, 28.75) * mm, "end": v(-320.61, -79.01) * mm});
            skLineSegment(sketch, "E101.bottom", {"start": v(-482.25, 190.4) * mm, "end": v(-428.37, 244.28) * mm});
            skLineSegment(sketch, "E101.top", {"start": v(-374.5, 82.63) * mm, "end": v(-320.61, 136.52) * mm});
            skLineSegment(sketch, "E101.left", {"start": v(-482.25, 190.4) * mm, "end": v(-374.5, 82.63) * mm});
            skLineSegment(sketch, "E101.right", {"start": v(-428.37, 244.28) * mm, "end": v(-320.61, 136.52) * mm});
            skLineSegment(sketch, "E102.bottom", {"start": v(-482.25, 82.63) * mm, "end": v(-428.37, 136.52) * mm});
            skLineSegment(sketch, "E102.top", {"start": v(-374.5, -25.13) * mm, "end": v(-320.61, 28.75) * mm});
            skLineSegment(sketch, "E102.left", {"start": v(-482.25, 82.63) * mm, "end": v(-374.5, -25.13) * mm});
            skLineSegment(sketch, "E102.right", {"start": v(-428.37, 136.52) * mm, "end": v(-320.61, 28.75) * mm});
            skLineSegment(sketch, "E103.bottom", {"start": v(-482.25, -132.9) * mm, "end": v(-428.37, -79.01) * mm});
            skLineSegment(sketch, "E103.top", {"start": v(-374.5, -240.66) * mm, "end": v(-320.61, -186.77) * mm});
            skLineSegment(sketch, "E103.left", {"start": v(-482.25, -132.9) * mm, "end": v(-374.5, -240.66) * mm});
            skLineSegment(sketch, "E103.right", {"start": v(-428.37, -79.01) * mm, "end": v(-320.61, -186.77) * mm});
            skLineSegment(sketch, "E104.bottom", {"start": v(-482.29, -240.63) * mm, "end": v(-428.4, -186.74) * mm});
            skLineSegment(sketch, "E104.top", {"start": v(-374.52, -348.39) * mm, "end": v(-320.64, -294.5) * mm});
            skLineSegment(sketch, "E104.left", {"start": v(-482.29, -240.63) * mm, "end": v(-374.52, -348.39) * mm});
            skLineSegment(sketch, "E104.right", {"start": v(-428.4, -186.74) * mm, "end": v(-320.64, -294.5) * mm});
            skLineSegment(sketch, "E105.bottom", {"start": v(-482.29, -563.91) * mm, "end": v(-428.4, -510.03) * mm});
            skLineSegment(sketch, "E105.top", {"start": v(-374.52, -671.68) * mm, "end": v(-320.64, -617.8) * mm});
            skLineSegment(sketch, "E105.left", {"start": v(-482.29, -563.91) * mm, "end": v(-374.52, -671.68) * mm});
            skLineSegment(sketch, "E105.right", {"start": v(-428.4, -510.03) * mm, "end": v(-320.64, -617.8) * mm});
            skLineSegment(sketch, "E106.bottom", {"start": v(-482.29, -348.39) * mm, "end": v(-428.4, -294.5) * mm});
            skLineSegment(sketch, "E106.top", {"start": v(-374.52, -456.15) * mm, "end": v(-320.64, -402.27) * mm});
            skLineSegment(sketch, "E106.left", {"start": v(-482.29, -348.39) * mm, "end": v(-374.52, -456.15) * mm});
            skLineSegment(sketch, "E106.right", {"start": v(-428.4, -294.5) * mm, "end": v(-320.64, -402.27) * mm});
            skLineSegment(sketch, "E107.bottom", {"start": v(-482.29, -456.15) * mm, "end": v(-428.4, -402.27) * mm});
            skLineSegment(sketch, "E107.top", {"start": v(-374.52, -563.91) * mm, "end": v(-320.64, -510.03) * mm});
            skLineSegment(sketch, "E107.left", {"start": v(-482.29, -456.15) * mm, "end": v(-374.52, -563.91) * mm});
            skLineSegment(sketch, "E107.right", {"start": v(-428.4, -402.27) * mm, "end": v(-320.64, -510.03) * mm});
            skSolve(sketch);
        }
        {
            var Q0;
            {var subQ5=sQuery(id+"F3.wireOp",EDGE,"E79.bottom");Q0=makeQuery(id+"F3.imprint","IMPRINT",FACE,{"disambiguationData":[TD([[makeQuery(id+"F3.imprint","IMPRINT",EDGE,{"derivedFrom":subQ5}),1.0]])]});}
            var Q1;
            {var subQ5=sQuery(id+"F3.wireOp",EDGE,"E80.bottom");Q1=makeQuery(id+"F3.imprint","IMPRINT",FACE,{"disambiguationData":[TD([[makeQuery(id+"F3.imprint","IMPRINT",EDGE,{"derivedFrom":subQ5}),1.0]])]});}
            var Q2;
            {var subQ1=sQuery(id+"F3.wireOp",EDGE,"E102.top");Q2=makeQuery(id+"F3.imprint","IMPRINT",FACE,{"disambiguationData":[TD([[makeQuery(id+"F3.imprint","IMPRINT",EDGE,{"derivedFrom":subQ1}),1.0]])]});}
            var Q3;
            {var subQ1=sQuery(id+"F3.wireOp",EDGE,"E70.left");Q3=makeQuery(id+"F3.imprint","IMPRINT",FACE,{"disambiguationData":[TD([[makeQuery(id+"F3.imprint","IMPRINT",EDGE,{"derivedFrom":subQ1}),-1.0]])]});}
            var Q4;
            Q4=makeQuery(id+"F3.imprint","IMPRINT",FACE,{"disambiguationData":[TD([[makeQuery(id+"F3.imprint","IMPRINT",EDGE,{"derivedFrom":sQuery(id+"F3.wireOp",EDGE,"E68.left")}),-1.0]])]});
            var Q5;
            Q5=makeQuery(id+"F3.imprint","IMPRINT",FACE,{"disambiguationData":[TD([[makeQuery(id+"F3.imprint","IMPRINT",EDGE,{"derivedFrom":sQuery(id+"F3.wireOp",EDGE,"E71.top")}),-1.0]])]});
            var Q6;
            {var subQ1=sQuery(id+"F3.wireOp",EDGE,"E68.left");Q6=makeQuery(id+"F3.imprint","IMPRINT",FACE,{"disambiguationData":[TD([[makeQuery(id+"F3.imprint","IMPRINT",EDGE,{"derivedFrom":subQ1}),1.0]])]});}
            var Q7;
            Q7=makeQuery(id+"F3.imprint","IMPRINT",FACE,{"disambiguationData":[TD([[makeQuery(id+"F3.imprint","IMPRINT",EDGE,{"derivedFrom":sQuery(id+"F3.wireOp",EDGE,"E69.top")}),-1.0]])]});
            var Q8;
            {var subQ2=sQuery(id+"F3.wireOp",EDGE,"E72.bottom");Q8=makeQuery(id+"F3.imprint","IMPRINT",FACE,{"disambiguationData":[TD([[makeQuery(id+"F3.imprint","IMPRINT",EDGE,{"derivedFrom":subQ2}),1.0]])]});}
            var Q9;
            {var subQ5=sQuery(id+"F3.wireOp",EDGE,"E84.bottom");Q9=makeQuery(id+"F3.imprint","IMPRINT",FACE,{"disambiguationData":[TD([[makeQuery(id+"F3.imprint","IMPRINT",EDGE,{"derivedFrom":subQ5}),1.0]])]});}
            var Q10;
            {var subQ0=sQuery(id+"F3.wireOp",EDGE,"E84.right");Q10=makeQuery(id+"F3.imprint","IMPRINT",FACE,{"disambiguationData":[TD([[makeQuery(id+"F3.imprint","IMPRINT",EDGE,{"derivedFrom":subQ0}),-1.0]])]});}
            var Q11;
            {var subQ5=sQuery(id+"F3.wireOp",EDGE,"E42.left");Q11=makeQuery(id+"F3.imprint","IMPRINT",FACE,{"disambiguationData":[TD([[makeQuery(id+"F3.imprint","IMPRINT",EDGE,{"derivedFrom":subQ5}),-1.0]])]});}
            var Q12;
            {var subQ1=sQuery(id+"F3.wireOp",EDGE,"E35.left");Q12=makeQuery(id+"F3.imprint","IMPRINT",FACE,{"disambiguationData":[TD([[makeQuery(id+"F3.imprint","IMPRINT",EDGE,{"derivedFrom":subQ1}),-1.0]])]});}
            var Q13;
            Q13=makeQuery(id+"F3.imprint","IMPRINT",FACE,{"disambiguationData":[TD([[makeQuery(id+"F3.imprint","IMPRINT",EDGE,{"derivedFrom":sQuery(id+"F3.wireOp",EDGE,"E33.left")}),-1.0]])]});
            var Q14;
            Q14=makeQuery(id+"F3.imprint","IMPRINT",FACE,{"disambiguationData":[TD([[makeQuery(id+"F3.imprint","IMPRINT",EDGE,{"derivedFrom":sQuery(id+"F3.wireOp",EDGE,"E36.top")}),-1.0]])]});
            var Q15;
            Q15=makeQuery(id+"F3.imprint","IMPRINT",FACE,{"disambiguationData":[TD([[makeQuery(id+"F3.imprint","IMPRINT",EDGE,{"derivedFrom":sQuery(id+"F3.wireOp",EDGE,"E34.top")}),-1.0]])]});
            var Q16;
            {var subQ2=sQuery(id+"F3.wireOp",EDGE,"E34.left");Q16=makeQuery(id+"F3.imprint","IMPRINT",FACE,{"disambiguationData":[TD([[makeQuery(id+"F3.imprint","IMPRINT",EDGE,{"derivedFrom":subQ2}),1.0]])]});}
            var Q17;
            {var subQ1=sQuery(id+"F3.wireOp",EDGE,"E33.left");Q17=makeQuery(id+"F3.imprint","IMPRINT",FACE,{"disambiguationData":[TD([[makeQuery(id+"F3.imprint","IMPRINT",EDGE,{"derivedFrom":subQ1}),1.0]])]});}
            var Q18;
            {var subQ6=sQuery(id+"F3.wireOp",EDGE,"E44.bottom");Q18=makeQuery(id+"F3.imprint","IMPRINT",FACE,{"disambiguationData":[TD([[makeQuery(id+"F3.imprint","IMPRINT",EDGE,{"derivedFrom":subQ6}),1.0]])]});}
            var Q19;
            {var subQ4=sQuery(id+"F3.wireOp",EDGE,"E45.bottom");Q19=makeQuery(id+"F3.imprint","IMPRINT",FACE,{"disambiguationData":[TD([[makeQuery(id+"F3.imprint","IMPRINT",EDGE,{"derivedFrom":subQ4}),1.0]])]});}
            var Q20;
            {var subQ1=sQuery(id+"F3.wireOp",EDGE,"E74.top");Q20=makeQuery(id+"F3.imprint","IMPRINT",FACE,{"disambiguationData":[TD([[makeQuery(id+"F3.imprint","IMPRINT",EDGE,{"derivedFrom":subQ1}),-1.0]])]});}
            var Q21;
            {var subQ1=sQuery(id+"F3.wireOp",EDGE,"E69.left");Q21=makeQuery(id+"F3.imprint","IMPRINT",FACE,{"disambiguationData":[TD([[makeQuery(id+"F3.imprint","IMPRINT",EDGE,{"derivedFrom":subQ1}),1.0]])]});}
            var Q22;
            {var subQ0=sQuery(id+"F3.wireOp",EDGE,"E76.left");Q22=makeQuery(id+"F3.imprint","IMPRINT",FACE,{"disambiguationData":[TD([[makeQuery(id+"F3.imprint","IMPRINT",EDGE,{"derivedFrom":subQ0}),-1.0]])]});}
            var Q23;
            {var subQ1=sQuery(id+"F3.wireOp",EDGE,"E31.left");var subQ3=makeQuery(id+"F1.opExtrude","CAP_EDGE",EDGE,{"disambiguationData":[OSD([sQuery(id+"F0.wireOp",EDGE,"E0.top")])],"isStart":false});var subQ4=makeQuery(id+"F3.imprint","INTERSECT",VERTEX,{"derivedFrom":[subQ3,subQ1]});Q23=makeQuery(id+"F3.imprint","IMPRINT",FACE,{"disambiguationData":[TD([[makeQuery(id+"F3.imprint","IMPRINT",EDGE,{"disambiguationData":[TD([[subQ4,-1.0]])],"derivedFrom":subQ3}),-1.0]])]});}
            var Q24;
            {var subQ0=sQuery(id+"F3.wireOp",EDGE,"E74.left");var subQ1=sQuery(id+"F3.wireOp",EDGE,"E73.top");var subQ2=makeQuery(id+"F3.imprint","INTERSECT",VERTEX,{"derivedFrom":[subQ1,subQ0]});Q24=makeQuery(id+"F3.imprint","IMPRINT",FACE,{"disambiguationData":[TD([[makeQuery(id+"F3.imprint","IMPRINT",EDGE,{"disambiguationData":[TD([[subQ2,1.0]])],"derivedFrom":subQ1}),-1.0]])]});}
            var Q25;
            {var subQ1=sQuery(id+"F3.wireOp",EDGE,"E66.left");var subQ3=makeQuery(id+"F1.opExtrude","CAP_EDGE",EDGE,{"disambiguationData":[OSD([sQuery(id+"F0.wireOp",EDGE,"E0.top")])],"isStart":false});var subQ4=makeQuery(id+"F3.imprint","INTERSECT",VERTEX,{"derivedFrom":[subQ3,subQ1]});Q25=makeQuery(id+"F3.imprint","IMPRINT",FACE,{"disambiguationData":[TD([[makeQuery(id+"F3.imprint","IMPRINT",EDGE,{"disambiguationData":[TD([[subQ4,-1.0]])],"derivedFrom":subQ3}),-1.0]])]});}
            var Q26;
            {var subQ1=sQuery(id+"F3.wireOp",EDGE,"E101.top");Q26=makeQuery(id+"F3.imprint","IMPRINT",FACE,{"disambiguationData":[TD([[makeQuery(id+"F3.imprint","IMPRINT",EDGE,{"derivedFrom":subQ1}),1.0]])]});}
            var Q27;
            {var subQ0=sQuery(id+"F3.wireOp",EDGE,"E101.right");var subQ1=sQuery(id+"F3.wireOp",EDGE,"E78.left");var subQ2=makeQuery(id+"F3.imprint","INTERSECT",VERTEX,{"derivedFrom":[subQ1,sQuery(id+"F3.wireOp",EDGE,"E101.top"),subQ0]});Q27=makeQuery(id+"F3.imprint","IMPRINT",FACE,{"disambiguationData":[TD([[makeQuery(id+"F3.imprint","IMPRINT",EDGE,{"disambiguationData":[TD([[subQ2,1.0]])],"derivedFrom":subQ1}),-1.0]])]});}
            var Q28;
            {var subQ5=sQuery(id+"F3.wireOp",EDGE,"E77.left");Q28=makeQuery(id+"F3.imprint","IMPRINT",FACE,{"disambiguationData":[TD([[makeQuery(id+"F3.imprint","IMPRINT",EDGE,{"derivedFrom":subQ5}),-1.0]])]});}
            var Q29;
            {var subQ0=sQuery(id+"F3.wireOp",EDGE,"E41.left");var subQ1=sQuery(id+"F3.wireOp",EDGE,"E41.top");var subQ2=makeQuery(id+"F3.imprint","INTERSECT",VERTEX,{"derivedFrom":[sQuery(id+"F3.wireOp",EDGE,"E36.right"),subQ1,subQ0]});Q29=makeQuery(id+"F3.imprint","IMPRINT",FACE,{"disambiguationData":[TD([[makeQuery(id+"F3.imprint","IMPRINT",EDGE,{"disambiguationData":[TD([[subQ2,-1.0]])],"derivedFrom":subQ1}),-1.0]])]});}
            var Q30;
            {var subQ0=sQuery(id+"F3.wireOp",EDGE,"E37.left");var subQ1=sQuery(id+"F3.wireOp",EDGE,"E37.top");var subQ2=makeQuery(id+"F3.imprint","INTERSECT",VERTEX,{"derivedFrom":[sQuery(id+"F3.wireOp",EDGE,"E36.left"),subQ1,subQ0]});Q30=makeQuery(id+"F3.imprint","IMPRINT",FACE,{"disambiguationData":[TD([[makeQuery(id+"F3.imprint","IMPRINT",EDGE,{"disambiguationData":[TD([[subQ2,-1.0]])],"derivedFrom":subQ1}),-1.0]])]});}
            var Q31;
            {var subQ0=sQuery(id+"F3.wireOp",EDGE,"E39.left");var subQ1=sQuery(id+"F3.wireOp",EDGE,"E39.top");var subQ2=makeQuery(id+"F3.imprint","INTERSECT",VERTEX,{"derivedFrom":[sQuery(id+"F3.wireOp",EDGE,"E34.left"),subQ1,subQ0]});Q31=makeQuery(id+"F3.imprint","IMPRINT",FACE,{"disambiguationData":[TD([[makeQuery(id+"F3.imprint","IMPRINT",EDGE,{"disambiguationData":[TD([[subQ2,-1.0]])],"derivedFrom":subQ1}),-1.0]])]});}
            var Q32;
            {var subQ0=sQuery(id+"F3.wireOp",EDGE,"E97.left");var subQ1=sQuery(id+"F3.wireOp",EDGE,"E97.bottom");var subQ2=makeQuery(id+"F3.imprint","INTERSECT",VERTEX,{"derivedFrom":[sQuery(id+"F3.wireOp",EDGE,"E84.right"),subQ1,subQ0]});Q32=makeQuery(id+"F3.imprint","IMPRINT",FACE,{"disambiguationData":[TD([[makeQuery(id+"F3.imprint","IMPRINT",EDGE,{"disambiguationData":[TD([[subQ2,-1.0]])],"derivedFrom":subQ1}),1.0]])]});}
            var Q33;
            {var subQ0=makeQuery(id+"F1.opExtrude","CAP_EDGE",EDGE,{"disambiguationData":[OSD([sQuery(id+"F0.wireOp",EDGE,"E4")])],"isStart":false});Q33=makeQuery(id+"F3.imprint","IMPRINT",FACE,{"disambiguationData":[TD([[makeQuery(id+"F3.imprint","IMPRINT",EDGE,{"derivedFrom":subQ0}),1.0]])]});}
            extrude(context, id + "F4", {"entities" : qUnion([Q0, Q1, Q2, Q3, Q4, Q5, Q6, Q7, Q8, Q9, Q10, Q11, Q12, Q13, Q14, Q15, Q16, Q17, Q18, Q19, Q20, Q21, Q22, Q23, Q24, Q25, Q26, Q27, Q28, Q29, Q30, Q31, Q32, Q33]), "operationType" : NewBodyOperationType.ADD, "depth" : 3.17 * mm, "offsetDistance" : 25.4 * mm});
        }
    });
